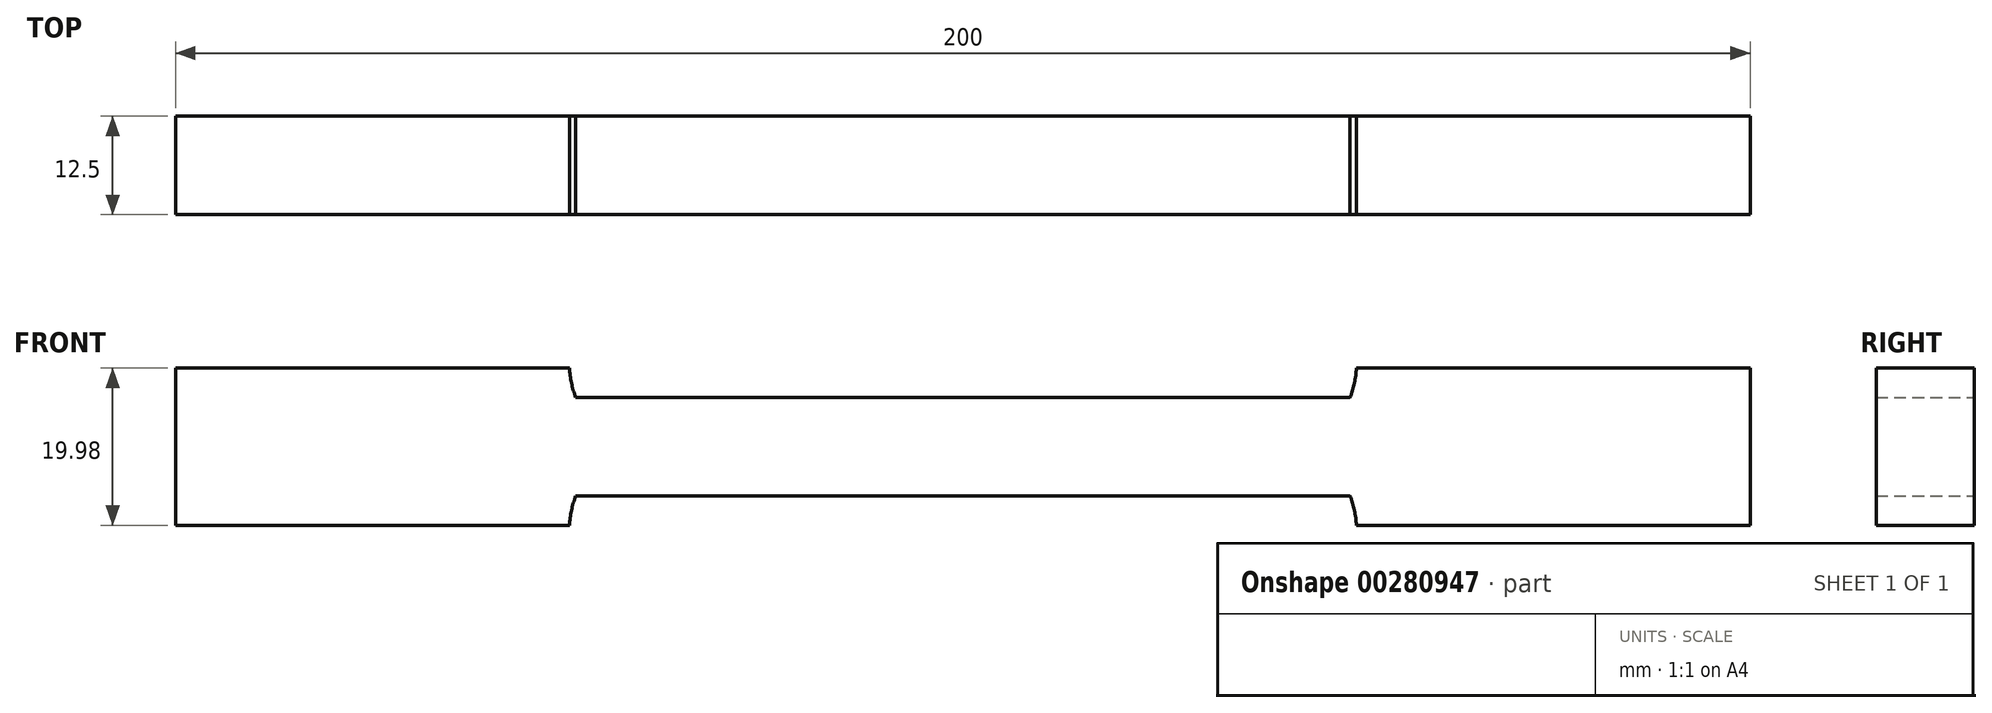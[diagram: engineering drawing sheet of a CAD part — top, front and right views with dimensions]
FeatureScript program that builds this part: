
annotation { "Feature Type Name" : "Feature", "Feature Type Description" : "" }
export const myFeature = defineFeature(function(context is Context, id is Id, definition is map)
    precondition{}
    {
        {
            var Q0;
            Q0=qCreatedBy(makeId("Front.planeOp"),FACE);
            var sketch = newSketch(context, id + "F0", { "sketchPlane" : qUnion([Q0])});
            skLineSegment(sketch, "E0", {"start": v(0, 6.25) * mm, "end": v(49.18, 6.25) * mm});
            skArc(sketch, "E1", {"start": v(49.18, 6.25) * mm, "mid": v(49.73, 8.1) * mm, "end": v(49.99, 10) * mm});
            skLineSegment(sketch, "E2", {"start": v(49.99, 10) * mm, "end": v(100, 10) * mm});
            skLineSegment(sketch, "E3", {"start": v(100, 10) * mm, "end": v(100, 0) * mm});
            skLineSegment(sketch, "E4.MirrorCS", {"start": v(0, -6.25) * mm, "end": v(49.18, -6.25) * mm});
            skLineSegment(sketch, "E5.MirrorCS", {"start": v(100, -10) * mm, "end": v(100, 0) * mm});
            skLineSegment(sketch, "E6.MirrorCS", {"start": v(49.99, -10) * mm, "end": v(100, -10) * mm});
            skArc(sketch, "E7.MirrorCS", {"start": v(49.18, -6.25) * mm, "mid": v(49.73, -8.1) * mm, "end": v(49.99, -10) * mm});
            skArc(sketch, "E8.MirrorCS", {"start": v(-49.18, -6.25) * mm, "mid": v(-49.73, -8.1) * mm, "end": v(-49.99, -10) * mm});
            skLineSegment(sketch, "E9.MirrorCS", {"start": v(-49.99, -10) * mm, "end": v(-100, -10) * mm});
            skLineSegment(sketch, "E10.MirrorCS", {"start": v(0, 6.25) * mm, "end": v(-49.18, 6.25) * mm});
            skArc(sketch, "E11.MirrorCS", {"start": v(-49.18, 6.25) * mm, "mid": v(-49.73, 8.1) * mm, "end": v(-49.99, 10) * mm});
            skLineSegment(sketch, "E12.MirrorCS", {"start": v(-49.99, 10) * mm, "end": v(-100, 10) * mm});
            skLineSegment(sketch, "E13.MirrorCS", {"start": v(-100, -10) * mm, "end": v(-100, 0) * mm});
            skLineSegment(sketch, "E14.MirrorCS", {"start": v(-100, 10) * mm, "end": v(-100, 0) * mm});
            skLineSegment(sketch, "E15.MirrorCS", {"start": v(0, -6.25) * mm, "end": v(-49.18, -6.25) * mm});
            skSolve(sketch);
        }
        {
            var Q0;
            Q0 = qSketchRegion(id + "F0", true);
            extrude(context, id + "F1", {"entities" : qUnion([Q0]), "endBound" : BoundingType.SYMMETRIC, "depth" : 12.5 * mm});
        }
    });
